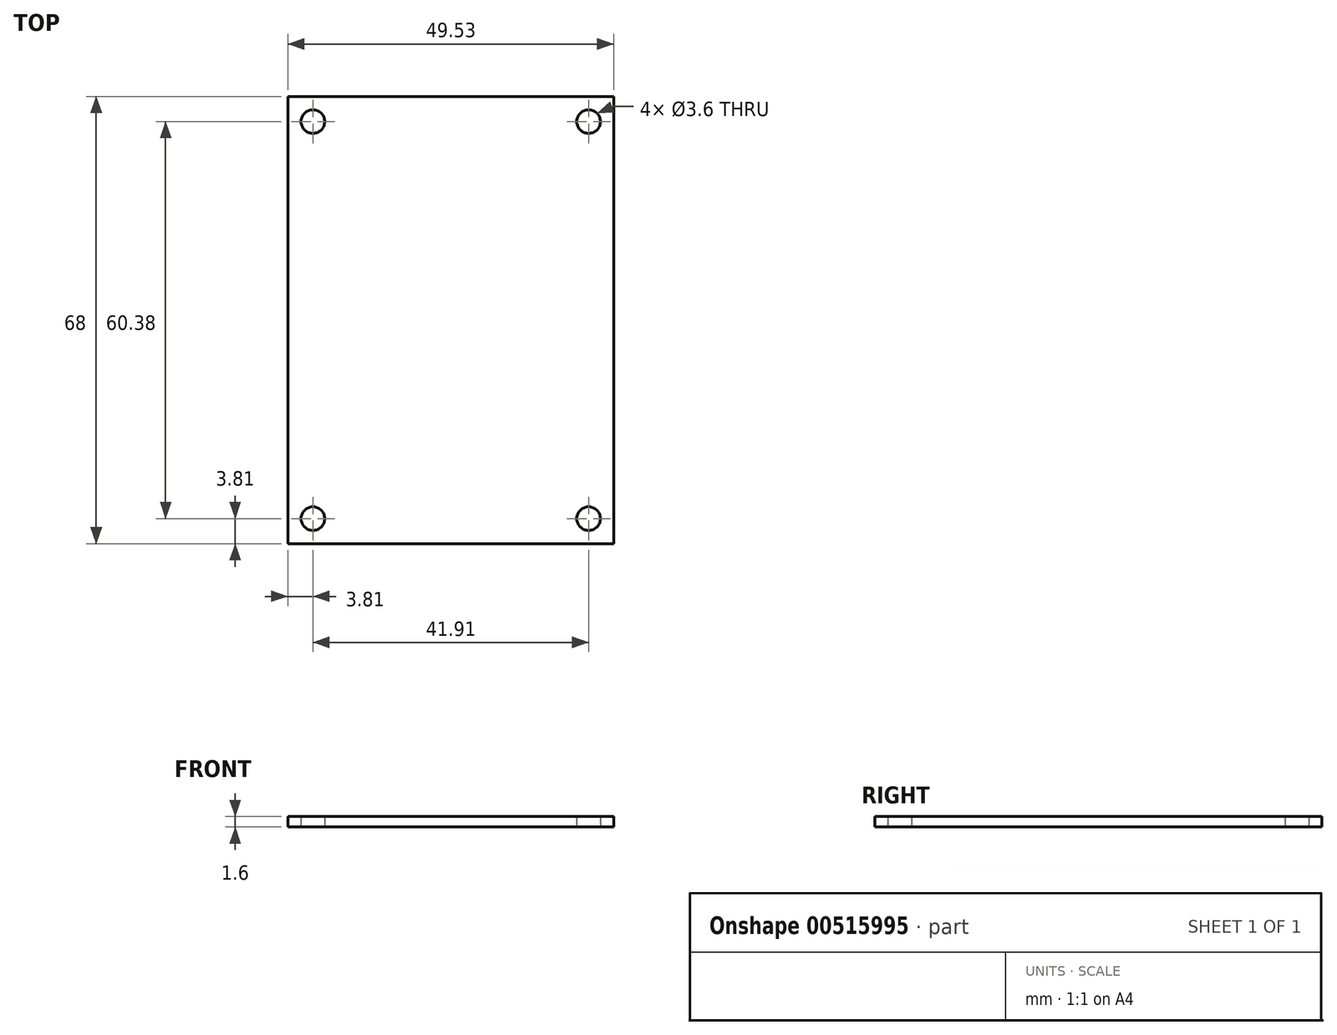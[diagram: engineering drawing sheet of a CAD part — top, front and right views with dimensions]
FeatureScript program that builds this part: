
annotation { "Feature Type Name" : "Feature", "Feature Type Description" : "" }
export const myFeature = defineFeature(function(context is Context, id is Id, definition is map)
    precondition{}
    {
        {
            var Q0;
            Q0=qCreatedBy(makeId("Top.planeOp"),FACE);
            var sketch = newSketch(context, id + "F0", { "sketchPlane" : qUnion([Q0])});
            skLineSegment(sketch, "E0.bottom", {"start": v(0, 0) * mm, "end": v(49.53, 0) * mm});
            skLineSegment(sketch, "E0.top", {"start": v(0, 68) * mm, "end": v(49.53, 68) * mm});
            skLineSegment(sketch, "E0.left", {"start": v(0, 0) * mm, "end": v(0, 68) * mm});
            skLineSegment(sketch, "E0.right", {"start": v(49.53, 0) * mm, "end": v(49.53, 68) * mm});
            skLineSegment(sketch, "E1", {"start": v(3.8, 64.2) * mm, "end": v(3.81, 3.8) * mm, "construction": true});
            skLineSegment(sketch, "E2", {"start": v(45.72, 3.81) * mm, "end": v(45.72, 64.2) * mm, "construction": true});
            skSolve(sketch);
        }
        {
            var Q0;
            Q0=makeQuery(id+"F0.imprint","IMPRINT",FACE,{"disambiguationData":[TD([[makeQuery(id+"F0.imprint","IMPRINT",EDGE,{"derivedFrom":sQuery(id+"F0.wireOp",EDGE,"E0.bottom")}),1.0]])]});
            extrude(context, id + "F1", {"entities" : qUnion([Q0]), "depth" : 1.6 * mm});
        }
        {
            var Q0;
            Q0=sQuery(id+"F0.wireOp",VERTEX,"E1.start");
            var Q1;
            Q1=sQuery(id+"F0.wireOp",VERTEX,"E2.end");
            var Q2;
            Q2=sQuery(id+"F0.wireOp",VERTEX,"E2.start");
            var Q3;
            Q3=sQuery(id+"F0.wireOp",VERTEX,"E1.end");
            var Q4;
            Q4=makeQuery(id+"F1.opExtrude","SWEPT_BODY",BODY,{"disambiguationData":[OSD([sQuery(id+"F0.wireOp",EDGE,"E0.bottom"),sQuery(id+"F0.wireOp",EDGE,"E0.top"),sQuery(id+"F0.wireOp",EDGE,"E0.left"),sQuery(id+"F0.wireOp",EDGE,"E0.right")])]});
            hole(context, id + "F2", {"style" : HoleStyle.SIMPLE, "endStyle" : HoleEndStyle.THROUGH, "oppositeDirection" : true, "holeDiameter" : 3.6 * mm, "isTappedThrough" : true, "tappedDepth" : 12 * mm, "tapClearance" : 3, "locations" : qUnion([Q0, Q1, Q2, Q3]), "scope" : qUnion([Q4])});
        }
    });
